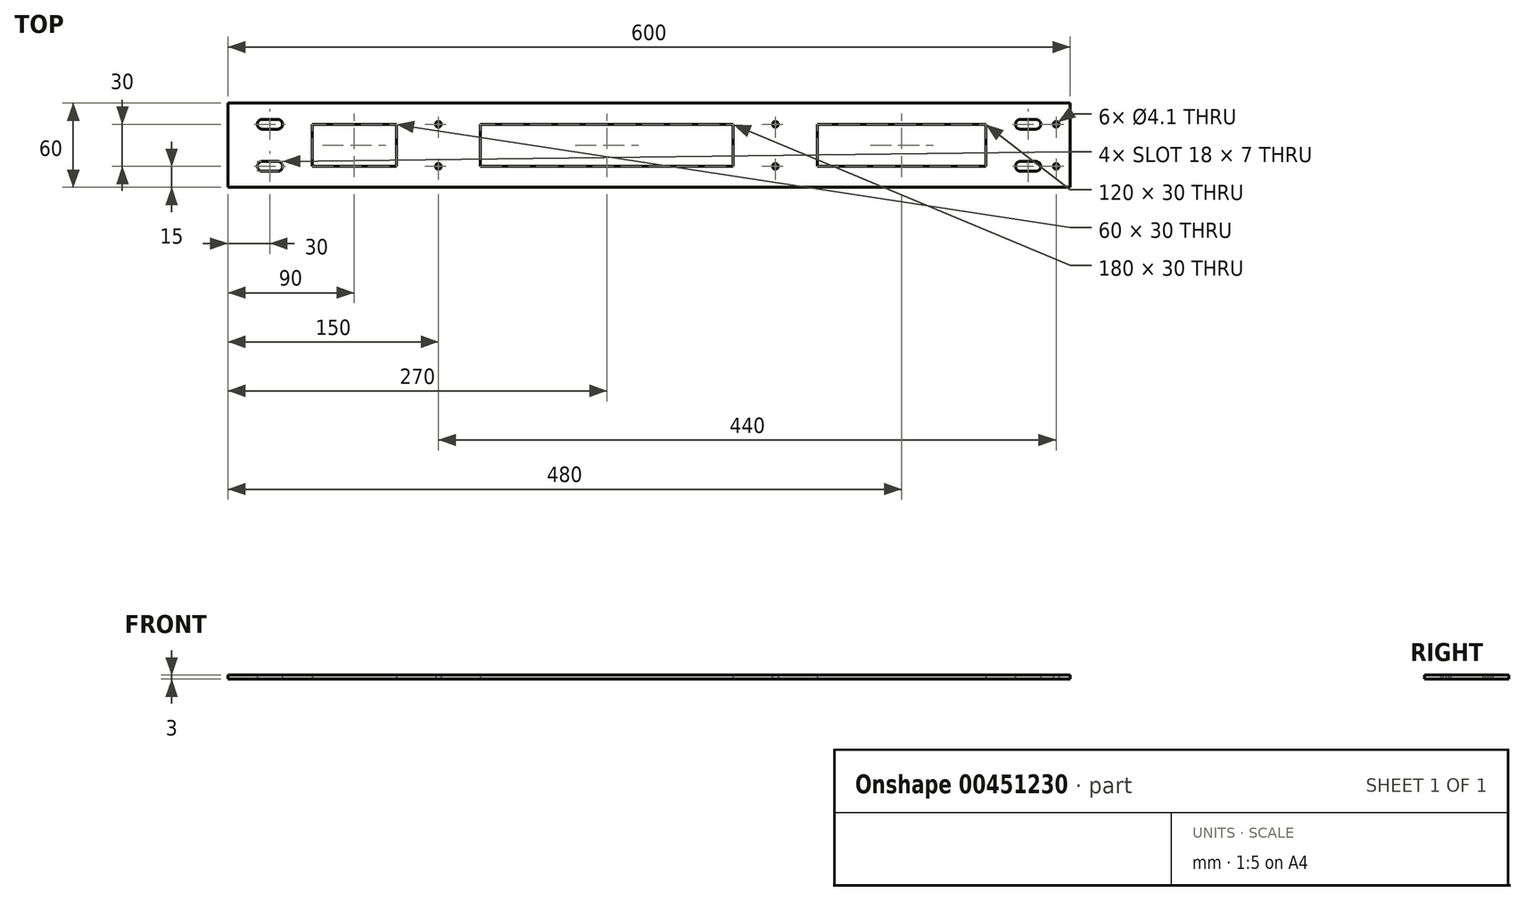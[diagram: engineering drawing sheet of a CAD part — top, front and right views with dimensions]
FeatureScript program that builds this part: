
annotation { "Feature Type Name" : "Feature", "Feature Type Description" : "" }
export const myFeature = defineFeature(function(context is Context, id is Id, definition is map)
    precondition{}
    {
        {
            var Q0;
            Q0=qCreatedBy(makeId("Top.planeOp"),FACE);
            var sketch = newSketch(context, id + "F0", { "sketchPlane" : qUnion([Q0])});
            skLineSegment(sketch, "E0.bottom", {"start": v(300, -30) * mm, "end": v(-300, -30) * mm});
            skLineSegment(sketch, "E0.top", {"start": v(300, 30) * mm, "end": v(-300, 30) * mm});
            skLineSegment(sketch, "E0.left", {"start": v(300, -30) * mm, "end": v(300, 30) * mm});
            skLineSegment(sketch, "E0.right", {"start": v(-300, -30) * mm, "end": v(-300, 30) * mm});
            skPoint(sketch, "E0.middle", {"position": v(0, 0) * mm});
            skLineSegment(sketch, "E1.bottom", {"start": v(-264.5, 11.5) * mm, "end": v(-275.5, 11.5) * mm});
            skLineSegment(sketch, "E1.top", {"start": v(-264.5, 18.5) * mm, "end": v(-275.5, 18.5) * mm});
            skLineSegment(sketch, "E1.left", {"start": v(-264.5, 11.5) * mm, "end": v(-264.5, 18.5) * mm, "construction": true});
            skLineSegment(sketch, "E1.right", {"start": v(-275.5, 11.5) * mm, "end": v(-275.5, 18.5) * mm, "construction": true});
            skPoint(sketch, "E1.middle", {"position": v(-270, 15) * mm});
            skArc(sketch, "E2", {"start": v(-275.5, 18.5) * mm, "mid": v(-279, 15) * mm, "end": v(-275.5, 11.5) * mm});
            skArc(sketch, "E3", {"start": v(-264.5, 11.5) * mm, "mid": v(-261, 15) * mm, "end": v(-264.5, 18.5) * mm});
            skCircle(sketch, "E4", {"center": v(-150, 15) * mm, "radius": 2.05 * mm});
            skCircle(sketch, "E5", {"center": v(90, 15) * mm, "radius": 2.05 * mm});
            skLineSegment(sketch, "E6.bottom", {"start": v(-120, 15) * mm, "end": v(60, 15) * mm});
            skLineSegment(sketch, "E6.top", {"start": v(-120, -15) * mm, "end": v(60, -15) * mm});
            skLineSegment(sketch, "E6.left", {"start": v(-120, 15) * mm, "end": v(-120, -15) * mm});
            skLineSegment(sketch, "E6.right", {"start": v(60, 15) * mm, "end": v(60, -15) * mm});
            skPoint(sketch, "E6.middle", {"position": v(-30, 0) * mm});
            skLineSegment(sketch, "E7.bottom", {"start": v(120, -15) * mm, "end": v(240, -15) * mm});
            skLineSegment(sketch, "E7.top", {"start": v(120, 15) * mm, "end": v(240, 15) * mm});
            skLineSegment(sketch, "E7.left", {"start": v(120, -15) * mm, "end": v(120, 15) * mm});
            skLineSegment(sketch, "E7.right", {"start": v(240, -15) * mm, "end": v(240, 15) * mm});
            skPoint(sketch, "E7.middle", {"position": v(180, 0) * mm});
            skLineSegment(sketch, "E8.bottom", {"start": v(-180, -15) * mm, "end": v(-240, -15) * mm});
            skLineSegment(sketch, "E8.top", {"start": v(-180, 15) * mm, "end": v(-240, 15) * mm});
            skLineSegment(sketch, "E8.left", {"start": v(-180, -15) * mm, "end": v(-180, 15) * mm});
            skLineSegment(sketch, "E8.right", {"start": v(-240, -15) * mm, "end": v(-240, 15) * mm});
            skPoint(sketch, "E8.middle", {"position": v(-210, 0) * mm});
            skCircle(sketch, "E9", {"center": v(290, 15) * mm, "radius": 2.05 * mm});
            skCircle(sketch, "E10", {"center": v(290, -15) * mm, "radius": 2.05 * mm});
            skCircle(sketch, "E11", {"center": v(90, -15) * mm, "radius": 2.05 * mm});
            skCircle(sketch, "E12", {"center": v(-150, -15) * mm, "radius": 2.05 * mm});
            skLineSegment(sketch, "E13.bottom", {"start": v(-264.5, -18.5) * mm, "end": v(-275.5, -18.5) * mm});
            skLineSegment(sketch, "E13.top", {"start": v(-264.5, -11.5) * mm, "end": v(-275.5, -11.5) * mm});
            skLineSegment(sketch, "E13.left", {"start": v(-264.5, -18.5) * mm, "end": v(-264.5, -11.5) * mm, "construction": true});
            skLineSegment(sketch, "E13.right", {"start": v(-275.5, -18.5) * mm, "end": v(-275.5, -11.5) * mm, "construction": true});
            skPoint(sketch, "E13.middle", {"position": v(-270, -15) * mm});
            skArc(sketch, "E14", {"start": v(-275.5, -11.5) * mm, "mid": v(-279, -15) * mm, "end": v(-275.5, -18.5) * mm});
            skArc(sketch, "E15", {"start": v(-264.5, -18.5) * mm, "mid": v(-261, -15) * mm, "end": v(-264.5, -11.5) * mm});
            skLineSegment(sketch, "E16.bottom", {"start": v(275.5, 11.5) * mm, "end": v(264.5, 11.5) * mm});
            skLineSegment(sketch, "E16.top", {"start": v(275.5, 18.5) * mm, "end": v(264.5, 18.5) * mm});
            skLineSegment(sketch, "E16.left", {"start": v(275.5, 11.5) * mm, "end": v(275.5, 18.5) * mm, "construction": true});
            skLineSegment(sketch, "E16.right", {"start": v(264.5, 11.5) * mm, "end": v(264.5, 18.5) * mm, "construction": true});
            skPoint(sketch, "E16.middle", {"position": v(270, 15) * mm});
            skArc(sketch, "E17", {"start": v(264.5, 18.5) * mm, "mid": v(261, 15) * mm, "end": v(264.5, 11.5) * mm});
            skArc(sketch, "E18", {"start": v(275.5, 11.5) * mm, "mid": v(279, 15) * mm, "end": v(275.5, 18.5) * mm});
            skLineSegment(sketch, "E19.bottom", {"start": v(275.5, -18.5) * mm, "end": v(264.5, -18.5) * mm});
            skLineSegment(sketch, "E19.top", {"start": v(275.5, -11.5) * mm, "end": v(264.5, -11.5) * mm});
            skLineSegment(sketch, "E19.left", {"start": v(275.5, -18.5) * mm, "end": v(275.5, -11.5) * mm, "construction": true});
            skLineSegment(sketch, "E19.right", {"start": v(264.5, -18.5) * mm, "end": v(264.5, -11.5) * mm, "construction": true});
            skPoint(sketch, "E19.middle", {"position": v(270, -15) * mm});
            skArc(sketch, "E20", {"start": v(264.5, -11.5) * mm, "mid": v(261, -15) * mm, "end": v(264.5, -18.5) * mm});
            skArc(sketch, "E21", {"start": v(275.5, -18.5) * mm, "mid": v(279, -15) * mm, "end": v(275.5, -11.5) * mm});
            skSolve(sketch);
        }
        {
            var Q0;
            Q0=qSketchRegion(id+"F0",true);
            extrude(context, id + "F1", {"entities" : qUnion([Q0]), "depth" : 3 * mm, "offsetDistance" : 25 * mm});
        }
    });
